# Revit family: Doors_Fire-Doors-Shutters_Wayne-Dalton_Insulated-Fire-Rated-Doors-FireStar-Model-700C
name_source: partatom
category: Specialty Equipment
units: mm (PartAtom-declared; Revit-internal decimal feet)

## family parameters
Always vertical = Yes
Classification Number = 23.30.10.21.34
Cut with Voids When Loaded = Yes
Enable Cutting in Views = No
Host = Wall
Maintain Annotation Orientation = No
Part Type = Normal
Room Calculation Point = No
Round Connector Dimension = Use Diameter
Shared = No

## types (6) — shared parameters
Connector Array Distance = 0"
Current = 20 A
Default Elevation = 0"
Description = FIRESTAR Model 700C Insulated Fire Door R-Value 5.0, U-Factor 0.2
Finish Material = Finish - Wayne Dalton - Black
Frequency = 60 Hz
Manufacturer = Wayne Dalton
Model = 700C
Operator Visibility = Yes
Powder Coat (Note) = Wayne Dalton also offers approximately 200 RAL powder coat options to complement the exterior colors of a building.
Power Factor = 1
Product Guid = 9f00e588-995a-41a3-b95e-30d0c432c3c2
Product Page URL = https://www.wayne-dalton.com
Product data url = https://www.bimobject.com
URL = https://www.wayne-dalton.com
Wall Closure = By host

## per-type parameters (varying)
| type | Apparent Load Phase 1 | Apparent Load Phase 2 | Apparent Load Phase 3 | Connector Array | Lift Up | Number of Poles | Voltage |
| 115 volts, one phase, 60 Hz (110-120V range) | 2300 VA | 0 VA | 0 VA | 3 | No | 1 | 115 V |
| Chain Hoist | 2300 VA | 0 VA | 0 VA | 2 | No | 1 | 115 V |
| Manual push-up | 2300 VA | 0 VA | 0 VA | 3 | Yes | 1 | 115 V |
| 230 volts, three phase, 60 Hz (208-245V range) | 2656 VA | 2656 VA | 2656 VA | 3 | No | 3 | 230 V |
| 230 volts, single phase, 60 Hz (208-245V range) | 4600 VA | 0 VA | 0 VA | 3 | No | 1 | 230 V |
| 460 volts, three phase, 60 Hz (456-495V range) | 5312 VA | 5312 VA | 5312 VA | 3 | No | 3 | 460 V |

type visibility flags (boolean, named after types; folded from table):
- 115 volts, one phase, 60 Hz (110-120V range): Yes: (none)
- Chain Hoist: Yes: Chain Hoist
- Manual push-up: Yes: (none)
- 230 volts, three phase, 60 Hz (208-245V range): Yes: (none)
- 230 volts, single phase, 60 Hz (208-245V range): Yes: (none)
- 460 volts, three phase, 60 Hz (456-495V range): Yes: (none)

## geometry (parser evidence)
native form markers: Sweep x13
no freeform markers — native parametric forms only
